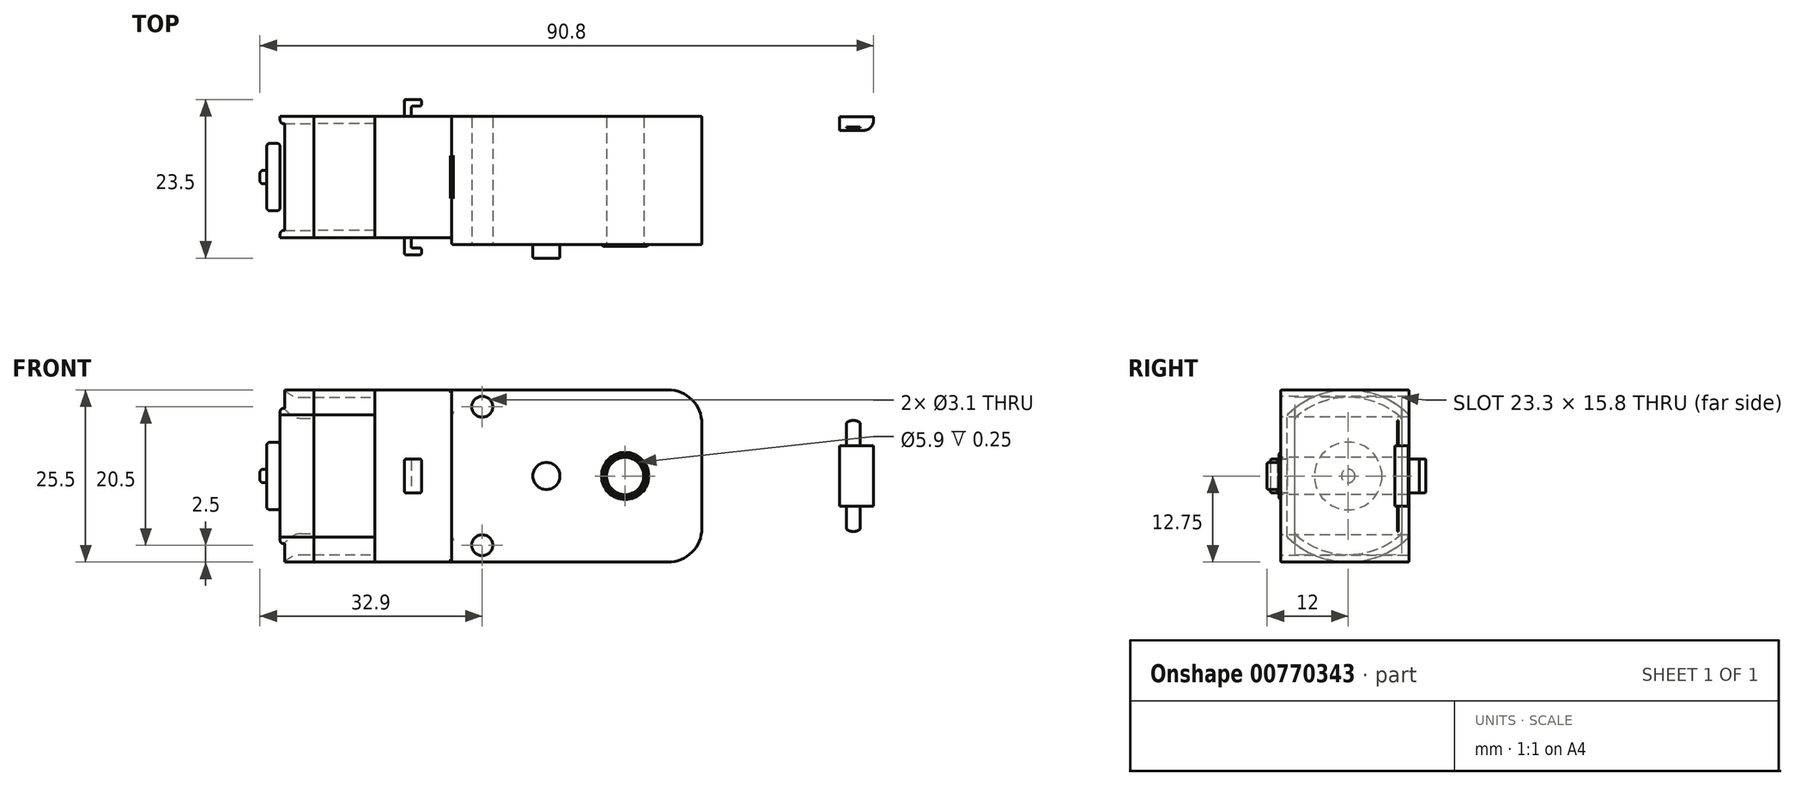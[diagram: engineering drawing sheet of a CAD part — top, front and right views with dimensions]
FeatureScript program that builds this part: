
annotation { "Feature Type Name" : "Feature", "Feature Type Description" : "" }
export const myFeature = defineFeature(function(context is Context, id is Id, definition is map)
    precondition{}
    {
        {
            var Q0;
            Q0=qCreatedBy(makeId("Front.planeOp"),FACE);
            var sketch = newSketch(context, id + "F0", { "sketchPlane" : qUnion([Q0])});
            skLineSegment(sketch, "E0.bottom", {"start": v(-18.5, 12.75) * mm, "end": v(18.5, 12.75) * mm});
            skLineSegment(sketch, "E0.top", {"start": v(-18.5, -12.75) * mm, "end": v(18.5, -12.75) * mm});
            skLineSegment(sketch, "E0.left", {"start": v(-18.5, 12.75) * mm, "end": v(-18.5, -12.75) * mm});
            skLineSegment(sketch, "E0.right", {"start": v(18.5, 12.75) * mm, "end": v(18.5, -12.75) * mm});
            skPoint(sketch, "E0.middle", {"position": v(0, 0) * mm});
            skSolve(sketch);
        }
        {
            var Q0;
            Q0=makeQuery(id+"F0.imprint","IMPRINT",FACE,{"disambiguationData":[TD([[makeQuery(id+"F0.imprint","IMPRINT",EDGE,{"derivedFrom":sQuery(id+"F0.wireOp",EDGE,"E0.bottom")}),-1.0]])]});
            extrude(context, id + "F1", {"entities" : qUnion([Q0]), "depth" : 19 * mm, "offsetDistance" : 25 * mm});
        }
        {
            var Q0;
            Q0=makeQuery(id+"F1.opExtrude","SWEPT_EDGE",EDGE,{"disambiguationData":[OSD([sQuery(id+"F0.wireOp",EDGE,"E0.bottom"),sQuery(id+"F0.wireOp",EDGE,"E0.right")])]});
            var Q1;
            Q1=makeQuery(id+"F1.opExtrude","SWEPT_EDGE",EDGE,{"disambiguationData":[OSD([sQuery(id+"F0.wireOp",EDGE,"E0.top"),sQuery(id+"F0.wireOp",EDGE,"E0.right")])]});
            fillet(context, id + "F2", {"entities" : qUnion([Q0, Q1]), "radius" : 5 * mm, "tangentPropagation" : true, "allowEdgeOverflow" : false});
        }
        {
            var Q0;
            Q0=makeQuery(id+"F1.opExtrude","SWEPT_FACE",FACE,{"disambiguationData":[OSD([sQuery(id+"F0.wireOp",EDGE,"E0.left")])]});
            var sketch = newSketch(context, id + "F3", { "sketchPlane" : qUnion([Q0])});
            skArc(sketch, "E1", {"start": v(0, 9.03) * mm, "mid": v(9, 12.75) * mm, "end": v(18, 9.03) * mm});
            skArc(sketch, "E2", {"start": v(0, -9.03) * mm, "mid": v(9, -12.75) * mm, "end": v(18, -9.03) * mm});
            skLineSegment(sketch, "E3", {"start": v(0, -9.03) * mm, "end": v(0, 9.03) * mm});
            skLineSegment(sketch, "E4", {"start": v(18, -9.03) * mm, "end": v(18, 9.03) * mm});
            skSolve(sketch);
        }
        {
            var Q0;
            {var subQ4=sQuery(id+"F3.wireOp",EDGE,"E3");Q0=makeQuery(id+"F3.imprint","IMPRINT",FACE,{"disambiguationData":[TD([[makeQuery(id+"F3.imprint","IMPRINT",EDGE,{"derivedFrom":subQ4}),1.0]])]});}
            extrude(context, id + "F4", {"entities" : qUnion([Q0]), "operationType" : NewBodyOperationType.ADD, "depth" : 11.4 * mm, "offsetDistance" : 25 * mm});
        }
        {
            var Q0;
            Q0=makeQuery(id+"F4.opExtrude","CAP_FACE",FACE,{"disambiguationData":[OSD([sQuery(id+"F3.wireOp",EDGE,"E1"),sQuery(id+"F3.wireOp",EDGE,"E2"),sQuery(id+"F3.wireOp",EDGE,"E3"),sQuery(id+"F3.wireOp",EDGE,"E4")])],"isStart":false});
            var sketch = newSketch(context, id + "F5", { "sketchPlane" : qUnion([Q0])});
            skArc(sketch, "E5.0", {"start": v(1.1, 8.56) * mm, "mid": v(9, 11.65) * mm, "end": v(16.9, 8.56) * mm});
            skLineSegment(sketch, "E5.1", {"start": v(1.1, 8.56) * mm, "end": v(1.1, -8.56) * mm});
            skArc(sketch, "E5.2", {"start": v(1.1, -8.56) * mm, "mid": v(9, -11.65) * mm, "end": v(16.9, -8.56) * mm});
            skLineSegment(sketch, "E5.3", {"start": v(16.9, -8.56) * mm, "end": v(16.9, 8.56) * mm});
            skSolve(sketch);
        }
        {
            var Q0;
            Q0=makeQuery(id+"F5.imprint","IMPRINT",FACE,{"disambiguationData":[TD([[makeQuery(id+"F5.imprint","IMPRINT",EDGE,{"derivedFrom":sQuery(id+"F5.wireOp",EDGE,"E5.0")}),-1.0]])]});
            extrude(context, id + "F6", {"entities" : qUnion([Q0]), "depth" : 9 * mm, "offsetDistance" : 25 * mm});
        }
        {
            var Q0;
            Q0=makeQuery(id+"F6.opExtrude","CAP_FACE",FACE,{"disambiguationData":[OSD([sQuery(id+"F5.wireOp",EDGE,"E5.0"),sQuery(id+"F5.wireOp",EDGE,"E5.1"),sQuery(id+"F5.wireOp",EDGE,"E5.2"),sQuery(id+"F5.wireOp",EDGE,"E5.3")])],"isStart":false});
            extrude(context, id + "F7", {"entities" : qUnion([Q0]), "depth" : 5 * mm, "offsetDistance" : 25 * mm});
        }
        {
            var Q0;
            Q0=makeQuery(id+"F7.opExtrude","CAP_EDGE",EDGE,{"disambiguationData":[OSD([sQuery(id+"F5.wireOp",EDGE,"E5.0")])],"isStart":false});
            var Q1;
            Q1=makeQuery(id+"F7.opExtrude","CAP_EDGE",EDGE,{"disambiguationData":[OSD([sQuery(id+"F5.wireOp",EDGE,"E5.2")])],"isStart":false});
            fillet(context, id + "F8", {"entities" : qUnion([Q0, Q1]), "radius" : 3 * mm, "tangentPropagation" : true, "allowEdgeOverflow" : false});
        }
        {
            var Q0;
            Q0=makeQuery(id+"F7.opExtrude","CAP_FACE",FACE,{"disambiguationData":[OSD([sQuery(id+"F5.wireOp",EDGE,"E5.0"),sQuery(id+"F5.wireOp",EDGE,"E5.1"),sQuery(id+"F5.wireOp",EDGE,"E5.2"),sQuery(id+"F5.wireOp",EDGE,"E5.3")])],"isStart":false});
            var sketch = newSketch(context, id + "F9", { "sketchPlane" : qUnion([Q0])});
            skCircle(sketch, "E6", {"center": v(9, 0) * mm, "radius": 5 * mm});
            skSolve(sketch);
        }
        {
            var Q0;
            Q0=makeQuery(id+"F9.imprint","IMPRINT",FACE,{"disambiguationData":[TD([[makeQuery(id+"F9.imprint","IMPRINT",EDGE,{"derivedFrom":sQuery(id+"F9.wireOp",EDGE,"E6")}),1.0]])]});
            extrude(context, id + "F10", {"entities" : qUnion([Q0]), "operationType" : NewBodyOperationType.ADD, "depth" : 2 * mm, "offsetDistance" : 25 * mm});
        }
        {
            var Q0;
            Q0=makeQuery(id+"F10.opExtrude","CAP_FACE",FACE,{"disambiguationData":[OSD([sQuery(id+"F9.wireOp",EDGE,"E6")])],"isStart":false});
            var sketch = newSketch(context, id + "F11", { "sketchPlane" : qUnion([Q0])});
            skCircle(sketch, "E7", {"center": v(9, 0) * mm, "radius": 1 * mm});
            skSolve(sketch);
        }
        {
            var Q0;
            Q0=makeQuery(id+"F11.imprint","IMPRINT",FACE,{"disambiguationData":[TD([[makeQuery(id+"F11.imprint","IMPRINT",EDGE,{"derivedFrom":sQuery(id+"F11.wireOp",EDGE,"E7")}),1.0]])]});
            extrude(context, id + "F12", {"entities" : qUnion([Q0]), "depth" : 1 * mm, "offsetDistance" : 25 * mm});
        }
        {
            var Q0;
            Q0=makeQuery(id+"F12.opExtrude","CAP_EDGE",EDGE,{"disambiguationData":[OSD([sQuery(id+"F11.wireOp",EDGE,"E7")])],"isStart":false});
            var Q1;
            Q1=makeQuery(id+"F10.opExtrude","CAP_EDGE",EDGE,{"disambiguationData":[OSD([sQuery(id+"F9.wireOp",EDGE,"E6")])],"isStart":false});
            var Q2;
            Q2=makeQuery(id+"F10.opExtrude","CAP_EDGE",EDGE,{"disambiguationData":[OSD([sQuery(id+"F9.wireOp",EDGE,"E6")])],"isStart":true});
            var Q3;
            Q3=makeQuery(id+"F7.opExtrude","CAP_EDGE",EDGE,{"disambiguationData":[OSD([sQuery(id+"F5.wireOp",EDGE,"E5.3")])],"isStart":false});
            var Q4;
            Q4=makeQuery(id+"F7.opExtrude","CAP_EDGE",EDGE,{"disambiguationData":[OSD([sQuery(id+"F5.wireOp",EDGE,"E5.1")])],"isStart":false});
            var Q5;
            Q5=makeQuery(id+"F6.opExtrude","SWEPT_EDGE",EDGE,{"disambiguationData":[OSD([sQuery(id+"F5.wireOp",EDGE,"E5.0"),sQuery(id+"F5.wireOp",EDGE,"E5.3")])]});
            var Q6;
            Q6=makeQuery(id+"F6.opExtrude","SWEPT_EDGE",EDGE,{"disambiguationData":[OSD([sQuery(id+"F5.wireOp",EDGE,"E5.0"),sQuery(id+"F5.wireOp",EDGE,"E5.1")])]});
            var Q7;
            Q7=makeQuery(id+"F6.opExtrude","SWEPT_EDGE",EDGE,{"disambiguationData":[OSD([sQuery(id+"F5.wireOp",EDGE,"E5.2"),sQuery(id+"F5.wireOp",EDGE,"E5.3")])]});
            var Q8;
            Q8=makeQuery(id+"F6.opExtrude","SWEPT_EDGE",EDGE,{"disambiguationData":[OSD([sQuery(id+"F5.wireOp",EDGE,"E5.1"),sQuery(id+"F5.wireOp",EDGE,"E5.2")])]});
            fillet(context, id + "F13", {"entities" : qUnion([Q0, Q1, Q2, Q3, Q4, Q5, Q6, Q7, Q8]), "radius" : 0.5 * mm, "tangentPropagation" : true, "allowEdgeOverflow" : false});
        }
        {
            var Q0;
            Q0=makeQuery(id+"F7.opExtrude","CAP_FACE",FACE,{"disambiguationData":[OSD([sQuery(id+"F5.wireOp",EDGE,"E5.0"),sQuery(id+"F5.wireOp",EDGE,"E5.1"),sQuery(id+"F5.wireOp",EDGE,"E5.2"),sQuery(id+"F5.wireOp",EDGE,"E5.3")])],"isStart":false});
            var sketch = newSketch(context, id + "F14", { "sketchPlane" : qUnion([Q0])});
            skArc(sketch, "E8", {"start": v(7.5, 9.65) * mm, "mid": v(9, 8.15) * mm, "end": v(10.5, 9.65) * mm});
            skArc(sketch, "E9", {"start": v(7.5, 11.55) * mm, "mid": v(9, 11.65) * mm, "end": v(10.5, 11.55) * mm});
            skLineSegment(sketch, "E10", {"start": v(7.5, 9.65) * mm, "end": v(7.5, 11.55) * mm});
            skLineSegment(sketch, "E11", {"start": v(10.5, 9.65) * mm, "end": v(10.5, 11.55) * mm});
            skLineSegment(sketch, "E12.MirrorCS", {"start": v(10.5, -9.65) * mm, "end": v(10.5, -11.55) * mm});
            skArc(sketch, "E13.MirrorCS", {"start": v(7.5, -9.65) * mm, "mid": v(9, -8.15) * mm, "end": v(10.5, -9.65) * mm});
            skLineSegment(sketch, "E14.MirrorCS", {"start": v(7.5, -9.65) * mm, "end": v(7.5, -11.55) * mm});
            skArc(sketch, "E15.MirrorCS", {"start": v(7.5, -11.55) * mm, "mid": v(9, -11.65) * mm, "end": v(10.5, -11.55) * mm});
            skSolve(sketch);
        }
        {
            var Q0;
            Q0=makeQuery(id+"F14.imprint","IMPRINT",FACE,{"disambiguationData":[TD([[makeQuery(id+"F14.imprint","IMPRINT",EDGE,{"derivedFrom":sQuery(id+"F14.wireOp",EDGE,"E9")}),-1.0]])]});
            var Q1;
            {var subQ0=sQuery(id+"F14.wireOp",EDGE,"E8");var subQ1=sQuery(id+"F5.wireOp",EDGE,"E5.0");var subQ2=makeQuery(id+"F8.opFillet","BLEND_EDGE",EDGE,{"blendedFrom":[makeQuery(id+"F7.opExtrude","CAP_EDGE",EDGE,{"disambiguationData":[OSD([subQ1])],"isStart":false}),makeQuery(id+"F7.opExtrude","CAP_FACE",FACE,{"disambiguationData":[OSD([subQ1,sQuery(id+"F5.wireOp",EDGE,"E5.1"),sQuery(id+"F5.wireOp",EDGE,"E5.2"),sQuery(id+"F5.wireOp",EDGE,"E5.3")])],"isStart":false})],"blendedInto":[makeQuery(id+"F7.opExtrude","CAP_FACE",FACE,{"disambiguationData":[OSD([subQ1,sQuery(id+"F5.wireOp",EDGE,"E5.1"),sQuery(id+"F5.wireOp",EDGE,"E5.2"),sQuery(id+"F5.wireOp",EDGE,"E5.3")])],"isStart":false})]});var subQ3=makeQuery(id+"F14.imprint","INTERSECT",VERTEX,{"disambiguationData":[OD(0.0)],"derivedFrom":[subQ2,subQ0]});Q1=makeQuery(id+"F14.imprint","IMPRINT",FACE,{"disambiguationData":[TD([[makeQuery(id+"F14.imprint","IMPRINT",EDGE,{"disambiguationData":[TD([[subQ3,-1.0]])],"derivedFrom":subQ0}),1.0]])]});}
            var Q2;
            {var subQ2=sQuery(id+"F14.wireOp",EDGE,"E12.MirrorCS");Q2=makeQuery(id+"F14.imprint","IMPRINT",FACE,{"disambiguationData":[TD([[makeQuery(id+"F14.imprint","IMPRINT",EDGE,{"derivedFrom":subQ2}),-1.0]])]});}
            var Q3;
            {var subQ0=sQuery(id+"F14.wireOp",EDGE,"E13.MirrorCS");var subQ1=sQuery(id+"F5.wireOp",EDGE,"E5.2");var subQ2=makeQuery(id+"F8.opFillet","BLEND_EDGE",EDGE,{"blendedFrom":[makeQuery(id+"F7.opExtrude","CAP_EDGE",EDGE,{"disambiguationData":[OSD([subQ1])],"isStart":false}),makeQuery(id+"F7.opExtrude","CAP_FACE",FACE,{"disambiguationData":[OSD([sQuery(id+"F5.wireOp",EDGE,"E5.0"),sQuery(id+"F5.wireOp",EDGE,"E5.1"),subQ1,sQuery(id+"F5.wireOp",EDGE,"E5.3")])],"isStart":false})],"blendedInto":[makeQuery(id+"F7.opExtrude","CAP_FACE",FACE,{"disambiguationData":[OSD([sQuery(id+"F5.wireOp",EDGE,"E5.0"),sQuery(id+"F5.wireOp",EDGE,"E5.1"),subQ1,sQuery(id+"F5.wireOp",EDGE,"E5.3")])],"isStart":false})]});var subQ3=makeQuery(id+"F14.imprint","INTERSECT",VERTEX,{"disambiguationData":[OD(0.0)],"derivedFrom":[subQ2,subQ0]});Q3=makeQuery(id+"F14.imprint","IMPRINT",FACE,{"disambiguationData":[TD([[makeQuery(id+"F14.imprint","IMPRINT",EDGE,{"disambiguationData":[TD([[subQ3,-1.0]])],"derivedFrom":subQ0}),-1.0]])]});}
            extrude(context, id + "F15", {"entities" : qUnion([Q0, Q1, Q2, Q3]), "operationType" : NewBodyOperationType.REMOVE, "oppositeDirection" : true, "depth" : 6 * mm, "offsetDistance" : 25 * mm});
        }
        {
            var Q0;
            Q0=makeQuery(id+"F7.opExtrude","SWEPT_FACE",FACE,{"disambiguationData":[OSD([sQuery(id+"F5.wireOp",EDGE,"E5.1")])]});
            var sketch = newSketch(context, id + "F16", { "sketchPlane" : qUnion([Q0])});
            skLineSegment(sketch, "E16", {"start": v(38.9, -4.5) * mm, "end": v(38.9, 4.5) * mm});
            skLineSegment(sketch, "E17", {"start": v(38.9, 4.5) * mm, "end": v(43.9, 4.5) * mm});
            skLineSegment(sketch, "E18", {"start": v(43.9, 4.5) * mm, "end": v(43.9, -4.5) * mm});
            skLineSegment(sketch, "E19", {"start": v(43.9, -4.5) * mm, "end": v(38.9, -4.5) * mm});
            skSolve(sketch);
        }
        {
            var Q0;
            {var subQ5=sQuery(id+"F16.wireOp",EDGE,"E16");Q0=makeQuery(id+"F16.imprint","IMPRINT",FACE,{"disambiguationData":[TD([[makeQuery(id+"F16.imprint","IMPRINT",EDGE,{"derivedFrom":subQ5}),1.0]])]});}
            var Q1;
            {var subQ1=sQuery(id+"F16.wireOp",EDGE,"E18");Q1=makeQuery(id+"F16.imprint","IMPRINT",FACE,{"disambiguationData":[TD([[makeQuery(id+"F16.imprint","IMPRINT",EDGE,{"derivedFrom":subQ1}),-1.0]])]});}
            extrude(context, id + "F17", {"entities" : qUnion([Q0, Q1]), "endBound" : BoundingType.SYMMETRIC, "depth" : 2 * mm, "offsetDistance" : 25 * mm});
        }
        {
            var Q0;
            Q0=makeQuery(id+"F17.opExtrude","CAP_EDGE",EDGE,{"disambiguationData":[OSD([sQuery(id+"F16.wireOp",EDGE,"E18")])],"isStart":false});
            fillet(context, id + "F18", {"entities" : qUnion([Q0]), "radius" : 1.5 * mm, "tangentPropagation" : true, "allowEdgeOverflow" : false});
        }
        {
            var Q0;
            Q0=makeQuery(id+"F7.opExtrude","SWEPT_FACE",FACE,{"disambiguationData":[OSD([sQuery(id+"F5.wireOp",EDGE,"E5.1")])]});
            cPlane(context, id + "F19", {"entities" : qUnion([Q0]), "cplaneType" : CPlaneType.OFFSET, "offset" : 0.5 * mm, "width" : 150 * mm, "height" : 150 * mm});
        }
        {
            var Q0;
            Q0=qCreatedBy(id+"F19.planeOp",FACE);
            var sketch = newSketch(context, id + "F20", { "sketchPlane" : qUnion([Q0])});
            skLineSegment(sketch, "E20.bottom", {"start": v(39.9, 4.5) * mm, "end": v(41.9, 4.5) * mm});
            skLineSegment(sketch, "E20.left", {"start": v(39.9, 4.5) * mm, "end": v(39.9, 7.85) * mm});
            skLineSegment(sketch, "E20.right", {"start": v(41.9, 4.5) * mm, "end": v(41.9, 7.85) * mm});
            skArc(sketch, "E21", {"start": v(41.9, 7.85) * mm, "mid": v(40.9, 8.23) * mm, "end": v(39.9, 7.85) * mm});
            skLineSegment(sketch, "E22.MirrorCS", {"start": v(39.9, -4.5) * mm, "end": v(41.9, -4.5) * mm});
            skLineSegment(sketch, "E23.MirrorCS", {"start": v(39.9, -4.5) * mm, "end": v(39.9, -7.85) * mm});
            skArc(sketch, "E24.MirrorCS", {"start": v(41.9, -7.85) * mm, "mid": v(40.9, -8.23) * mm, "end": v(39.9, -7.85) * mm});
            skLineSegment(sketch, "E25.MirrorCS", {"start": v(41.9, -4.5) * mm, "end": v(41.9, -7.85) * mm});
            skSolve(sketch);
        }
        {
            var Q0;
            Q0=makeQuery(id+"F20.imprint","IMPRINT",FACE,{"disambiguationData":[TD([[makeQuery(id+"F20.imprint","IMPRINT",EDGE,{"derivedFrom":sQuery(id+"F20.wireOp",EDGE,"E20.bottom")}),1.0]])]});
            var Q1;
            Q1=makeQuery(id+"F20.imprint","IMPRINT",FACE,{"disambiguationData":[TD([[makeQuery(id+"F20.imprint","IMPRINT",EDGE,{"derivedFrom":sQuery(id+"F20.wireOp",EDGE,"E22.MirrorCS")}),-1.0]])]});
            extrude(context, id + "F21", {"entities" : qUnion([Q0, Q1]), "depth" : 0.1 * mm, "offsetDistance" : 25 * mm});
        }
        {
            var Q0;
            Q0=makeQuery(id+"F1.opExtrude","CAP_FACE",FACE,{"disambiguationData":[OSD([sQuery(id+"F0.wireOp",EDGE,"E0.bottom"),sQuery(id+"F0.wireOp",EDGE,"E0.top"),sQuery(id+"F0.wireOp",EDGE,"E0.left"),sQuery(id+"F0.wireOp",EDGE,"E0.right")])],"isStart":false});
            var sketch = newSketch(context, id + "F22", { "sketchPlane" : qUnion([Q0])});
            skCircle(sketch, "E26", {"center": v(-4.5, 0) * mm, "radius": 2 * mm});
            skSolve(sketch);
        }
        {
            var Q0;
            Q0=makeQuery(id+"F22.imprint","IMPRINT",FACE,{"disambiguationData":[TD([[makeQuery(id+"F22.imprint","IMPRINT",EDGE,{"derivedFrom":sQuery(id+"F22.wireOp",EDGE,"E26")}),1.0]])]});
            extrude(context, id + "F23", {"entities" : qUnion([Q0]), "operationType" : NewBodyOperationType.ADD, "depth" : 2 * mm, "offsetDistance" : 25 * mm});
        }
        {
            var Q0;
            Q0=makeQuery(id+"F1.opExtrude","CAP_FACE",FACE,{"disambiguationData":[OSD([sQuery(id+"F0.wireOp",EDGE,"E0.bottom"),sQuery(id+"F0.wireOp",EDGE,"E0.top"),sQuery(id+"F0.wireOp",EDGE,"E0.left"),sQuery(id+"F0.wireOp",EDGE,"E0.right")])],"isStart":false});
            var sketch = newSketch(context, id + "F24", { "sketchPlane" : qUnion([Q0])});
            skCircle(sketch, "E27", {"center": v(7.15, 0) * mm, "radius": 2.75 * mm});
            skPoint(sketch, "E28", {"position": v(-14, 10.25) * mm});
            skPoint(sketch, "E29", {"position": v(-14, -10.25) * mm});
            skSolve(sketch);
        }
        {
            var Q0;
            Q0=makeQuery(id+"F24.imprint","IMPRINT",FACE,{"disambiguationData":[TD([[makeQuery(id+"F24.imprint","IMPRINT",EDGE,{"derivedFrom":sQuery(id+"F24.wireOp",EDGE,"E27")}),1.0]])]});
            extrude(context, id + "F25", {"entities" : qUnion([Q0]), "operationType" : NewBodyOperationType.REMOVE, "endBound" : BoundingType.THROUGH_ALL, "oppositeDirection" : true, "depth" : 25 * mm, "offsetDistance" : 25 * mm});
        }
        {
            var Q0;
            Q0=sQuery(id+"F24.wireOp",VERTEX,"E28");
            var Q1;
            Q1=sQuery(id+"F24.wireOp",VERTEX,"E29");
            var Q2;
            Q2=makeQuery(id+"F1.opExtrude","SWEPT_BODY",BODY,{"disambiguationData":[OSD([sQuery(id+"F0.wireOp",EDGE,"E0.bottom"),sQuery(id+"F0.wireOp",EDGE,"E0.top"),sQuery(id+"F0.wireOp",EDGE,"E0.left"),sQuery(id+"F0.wireOp",EDGE,"E0.right")])]});
            hole(context, id + "F26", {"style" : HoleStyle.SIMPLE, "endStyle" : HoleEndStyle.THROUGH, "holeDiameter" : 3.1 * mm, "majorDiameter" : 5 * mm, "isTappedThrough" : true, "tappedDepth" : 12 * mm, "tapClearance" : 3, "locations" : qUnion([Q0, Q1]), "scope" : qUnion([Q2])});
        }
        {
            var Q0;
            Q0=qCreatedBy(makeId("Top.planeOp"),FACE);
            var sketch = newSketch(context, id + "F27", { "sketchPlane" : qUnion([Q0])});
            skLineSegment(sketch, "E30", {"start": v(-25.5, -18) * mm, "end": v(-25.5, -20.5) * mm});
            skLineSegment(sketch, "E31", {"start": v(-25.5, -20.5) * mm, "end": v(-23, -20.5) * mm});
            skLineSegment(sketch, "E32", {"start": v(-23, -20.5) * mm, "end": v(-23, -19.5) * mm});
            skLineSegment(sketch, "E33", {"start": v(-23, -19.5) * mm, "end": v(-24.5, -19.5) * mm});
            skLineSegment(sketch, "E34", {"start": v(-24.5, -19.5) * mm, "end": v(-24.5, -18) * mm});
            skLineSegment(sketch, "E35", {"start": v(-24.5, -18) * mm, "end": v(-25.5, -18) * mm});
            skLineSegment(sketch, "E36", {"start": v(-36.83, -9) * mm, "end": v(-23.9, -9) * mm});
            skLineSegment(sketch, "E37.MirrorCS", {"start": v(-24.5, 0) * mm, "end": v(-25.5, 0) * mm});
            skLineSegment(sketch, "E38.MirrorCS", {"start": v(-24.5, 1.5) * mm, "end": v(-24.5, 0) * mm});
            skLineSegment(sketch, "E39.MirrorCS", {"start": v(-23, 1.5) * mm, "end": v(-24.5, 1.5) * mm});
            skLineSegment(sketch, "E40.MirrorCS", {"start": v(-25.5, 0) * mm, "end": v(-25.5, 2.5) * mm});
            skLineSegment(sketch, "E41.MirrorCS", {"start": v(-23, 2.5) * mm, "end": v(-23, 1.5) * mm});
            skLineSegment(sketch, "E42.MirrorCS", {"start": v(-25.5, 2.5) * mm, "end": v(-23, 2.5) * mm});
            skSolve(sketch);
        }
        {
            var Q0;
            Q0=makeQuery(id+"F27.imprint","IMPRINT",FACE,{"disambiguationData":[TD([[makeQuery(id+"F27.imprint","IMPRINT",EDGE,{"derivedFrom":sQuery(id+"F27.wireOp",EDGE,"E30")}),1.0]])]});
            var Q1;
            Q1=makeQuery(id+"F27.imprint","IMPRINT",FACE,{"disambiguationData":[TD([[makeQuery(id+"F27.imprint","IMPRINT",EDGE,{"derivedFrom":sQuery(id+"F27.wireOp",EDGE,"E37.MirrorCS")}),-1.0]])]});
            extrude(context, id + "F28", {"entities" : qUnion([Q0, Q1]), "operationType" : NewBodyOperationType.ADD, "endBound" : BoundingType.SYMMETRIC, "depth" : 5 * mm, "offsetDistance" : 25 * mm});
        }
        {
            var Q0;
            Q0=makeQuery(id+"F4.boolean.opBoolean","MERGE",FACE,{"derivedFrom":[makeQuery(id+"F1.opExtrude","CAP_FACE",FACE,{"disambiguationData":[OSD([sQuery(id+"F0.wireOp",EDGE,"E0.bottom"),sQuery(id+"F0.wireOp",EDGE,"E0.top"),sQuery(id+"F0.wireOp",EDGE,"E0.left"),sQuery(id+"F0.wireOp",EDGE,"E0.right")])],"isStart":true}),makeQuery(id+"F4.opExtrude","SWEPT_FACE",FACE,{"disambiguationData":[OSD([sQuery(id+"F3.wireOp",EDGE,"E3")])]})]});
            var Q1;
            Q1=makeQuery(id+"F1.opExtrude","CAP_FACE",FACE,{"disambiguationData":[OSD([sQuery(id+"F0.wireOp",EDGE,"E0.bottom"),sQuery(id+"F0.wireOp",EDGE,"E0.top"),sQuery(id+"F0.wireOp",EDGE,"E0.left"),sQuery(id+"F0.wireOp",EDGE,"E0.right")])],"isStart":false});
            var Q2;
            Q2=makeQuery(id+"F4.opExtrude","SWEPT_FACE",FACE,{"disambiguationData":[OSD([sQuery(id+"F3.wireOp",EDGE,"E4")])]});
            var Q3;
            Q3=makeQuery(id+"F4.opExtrude","SWEPT_FACE",FACE,{"disambiguationData":[OSD([sQuery(id+"F3.wireOp",EDGE,"E1")])]});
            var Q4;
            Q4=makeQuery(id+"F4.opExtrude","SWEPT_FACE",FACE,{"disambiguationData":[OSD([sQuery(id+"F3.wireOp",EDGE,"E2")])]});
            var Q5;
            Q5=makeQuery(id+"F28.opExtrude","SWEPT_FACE",FACE,{"disambiguationData":[OSD([sQuery(id+"F27.wireOp",EDGE,"E42.MirrorCS")])]});
            var Q6;
            Q6=makeQuery(id+"F28.opExtrude","CAP_FACE",FACE,{"disambiguationData":[OSD([sQuery(id+"F27.wireOp",EDGE,"E37.MirrorCS"),sQuery(id+"F27.wireOp",EDGE,"E38.MirrorCS"),sQuery(id+"F27.wireOp",EDGE,"E39.MirrorCS"),sQuery(id+"F27.wireOp",EDGE,"E40.MirrorCS"),sQuery(id+"F27.wireOp",EDGE,"E41.MirrorCS"),sQuery(id+"F27.wireOp",EDGE,"E42.MirrorCS")])],"isStart":false});
            var Q7;
            Q7=makeQuery(id+"F28.opExtrude","CAP_FACE",FACE,{"disambiguationData":[OSD([sQuery(id+"F27.wireOp",EDGE,"E37.MirrorCS"),sQuery(id+"F27.wireOp",EDGE,"E38.MirrorCS"),sQuery(id+"F27.wireOp",EDGE,"E39.MirrorCS"),sQuery(id+"F27.wireOp",EDGE,"E40.MirrorCS"),sQuery(id+"F27.wireOp",EDGE,"E41.MirrorCS"),sQuery(id+"F27.wireOp",EDGE,"E42.MirrorCS")])],"isStart":true});
            var Q8;
            Q8=makeQuery(id+"F28.opExtrude","SWEPT_FACE",FACE,{"disambiguationData":[OSD([sQuery(id+"F27.wireOp",EDGE,"E39.MirrorCS")])]});
            var Q9;
            {var subQ0=sQuery(id+"F0.wireOp",EDGE,"E0.left");var subQ1=sQuery(id+"F0.wireOp",EDGE,"E0.top");Q9=makeQuery(id+"F4.boolean.opBoolean","SPLIT",EDGE,{"disambiguationData":[TD([makeQuery(id+"F1.opExtrude","CAP_FACE",FACE,{"disambiguationData":[OSD([sQuery(id+"F0.wireOp",EDGE,"E0.bottom"),subQ1,subQ0,sQuery(id+"F0.wireOp",EDGE,"E0.right")])],"isStart":false})])],"derivedFrom":makeQuery(id+"F1.opExtrude","SWEPT_EDGE",EDGE,{"disambiguationData":[OSD([subQ1,subQ0])]})});}
            var Q10;
            {var subQ0=sQuery(id+"F0.wireOp",EDGE,"E0.left");var subQ1=sQuery(id+"F0.wireOp",EDGE,"E0.top");Q10=makeQuery(id+"F4.boolean.opBoolean","SPLIT",EDGE,{"disambiguationData":[TD([makeQuery(id+"F4.opExtrude","SWEPT_FACE",FACE,{"disambiguationData":[OSD([sQuery(id+"F3.wireOp",EDGE,"E3")])]})])],"derivedFrom":makeQuery(id+"F1.opExtrude","SWEPT_EDGE",EDGE,{"disambiguationData":[OSD([subQ1,subQ0])]})});}
            var Q11;
            {var subQ0=sQuery(id+"F0.wireOp",EDGE,"E0.bottom");var subQ1=sQuery(id+"F0.wireOp",EDGE,"E0.left");Q11=makeQuery(id+"F4.boolean.opBoolean","SPLIT",EDGE,{"disambiguationData":[TD([makeQuery(id+"F1.opExtrude","CAP_FACE",FACE,{"disambiguationData":[OSD([subQ0,sQuery(id+"F0.wireOp",EDGE,"E0.top"),subQ1,sQuery(id+"F0.wireOp",EDGE,"E0.right")])],"isStart":false})])],"derivedFrom":makeQuery(id+"F1.opExtrude","SWEPT_EDGE",EDGE,{"disambiguationData":[OSD([subQ0,subQ1])]})});}
            var Q12;
            {var subQ0=sQuery(id+"F0.wireOp",EDGE,"E0.left");var subQ1=sQuery(id+"F0.wireOp",EDGE,"E0.bottom");Q12=makeQuery(id+"F4.boolean.opBoolean","SPLIT",EDGE,{"disambiguationData":[TD([makeQuery(id+"F4.opExtrude","SWEPT_FACE",FACE,{"disambiguationData":[OSD([sQuery(id+"F3.wireOp",EDGE,"E3")])]})])],"derivedFrom":makeQuery(id+"F1.opExtrude","SWEPT_EDGE",EDGE,{"disambiguationData":[OSD([subQ1,subQ0])]})});}
            var Q13;
            Q13=makeQuery(id+"F28.opExtrude","CAP_FACE",FACE,{"disambiguationData":[OSD([sQuery(id+"F27.wireOp",EDGE,"E30"),sQuery(id+"F27.wireOp",EDGE,"E31"),sQuery(id+"F27.wireOp",EDGE,"E32"),sQuery(id+"F27.wireOp",EDGE,"E33"),sQuery(id+"F27.wireOp",EDGE,"E34"),sQuery(id+"F27.wireOp",EDGE,"E35")])],"isStart":false});
            var Q14;
            Q14=makeQuery(id+"F28.opExtrude","CAP_FACE",FACE,{"disambiguationData":[OSD([sQuery(id+"F27.wireOp",EDGE,"E30"),sQuery(id+"F27.wireOp",EDGE,"E31"),sQuery(id+"F27.wireOp",EDGE,"E32"),sQuery(id+"F27.wireOp",EDGE,"E33"),sQuery(id+"F27.wireOp",EDGE,"E34"),sQuery(id+"F27.wireOp",EDGE,"E35")])],"isStart":true});
            var Q15;
            Q15=makeQuery(id+"F28.opExtrude","SWEPT_EDGE",EDGE,{"disambiguationData":[OSD([sQuery(id+"F27.wireOp",EDGE,"E30"),sQuery(id+"F27.wireOp",EDGE,"E31")])]});
            var Q16;
            Q16=makeQuery(id+"F28.opExtrude","SWEPT_EDGE",EDGE,{"disambiguationData":[OSD([sQuery(id+"F27.wireOp",EDGE,"E31"),sQuery(id+"F27.wireOp",EDGE,"E32")])]});
            var Q17;
            Q17=makeQuery(id+"F28.opExtrude","SWEPT_EDGE",EDGE,{"disambiguationData":[OSD([sQuery(id+"F27.wireOp",EDGE,"E32"),sQuery(id+"F27.wireOp",EDGE,"E33")])]});
            var Q18;
            Q18=makeQuery(id+"F28.opExtrude","SWEPT_EDGE",EDGE,{"disambiguationData":[OSD([sQuery(id+"F27.wireOp",EDGE,"E33"),sQuery(id+"F27.wireOp",EDGE,"E34")])]});
            var Q19;
            Q19=makeQuery(id+"F23.opExtrude","CAP_EDGE",EDGE,{"disambiguationData":[OSD([sQuery(id+"F22.wireOp",EDGE,"E26")])],"isStart":false});
            fillet(context, id + "F29", {"entities" : qUnion([Q0, Q1, Q2, Q3, Q4, Q5, Q6, Q7, Q8, Q9, Q10, Q11, Q12, Q13, Q14, Q15, Q16, Q17, Q18, Q19]), "radius" : 0.2 * mm, "tangentPropagation" : true, "allowEdgeOverflow" : false});
        }
        {
            var Q0;
            Q0=makeQuery(id+"F1.opExtrude","CAP_FACE",FACE,{"disambiguationData":[OSD([sQuery(id+"F0.wireOp",EDGE,"E0.bottom"),sQuery(id+"F0.wireOp",EDGE,"E0.top"),sQuery(id+"F0.wireOp",EDGE,"E0.left"),sQuery(id+"F0.wireOp",EDGE,"E0.right")])],"isStart":false});
            var sketch = newSketch(context, id + "F30", { "sketchPlane" : qUnion([Q0])});
            skCircle(sketch, "E43", {"center": v(7.15, 0) * mm, "radius": 3.5 * mm});
            skSolve(sketch);
        }
        {
            var Q0;
            Q0=makeQuery(id+"F30.imprint","IMPRINT",FACE,{"disambiguationData":[TD([[makeQuery(id+"F30.imprint","IMPRINT",EDGE,{"derivedFrom":sQuery(id+"F30.wireOp",EDGE,"E43")}),1.0]])]});
            extrude(context, id + "F31", {"entities" : qUnion([Q0]), "operationType" : NewBodyOperationType.ADD, "depth" : 0.25 * mm, "offsetDistance" : 25 * mm});
        }
        {
            var Q0;
            Q0=makeQuery(id+"F31.opExtrude","CAP_EDGE",EDGE,{"disambiguationData":[OSD([sQuery(id+"F30.wireOp",EDGE,"E43")])],"isStart":false});
            chamfer(context, id + "F32", {"entities" : qUnion([Q0]), "width" : 0.25 * mm, "tangentPropagation" : true});
        }
    });
